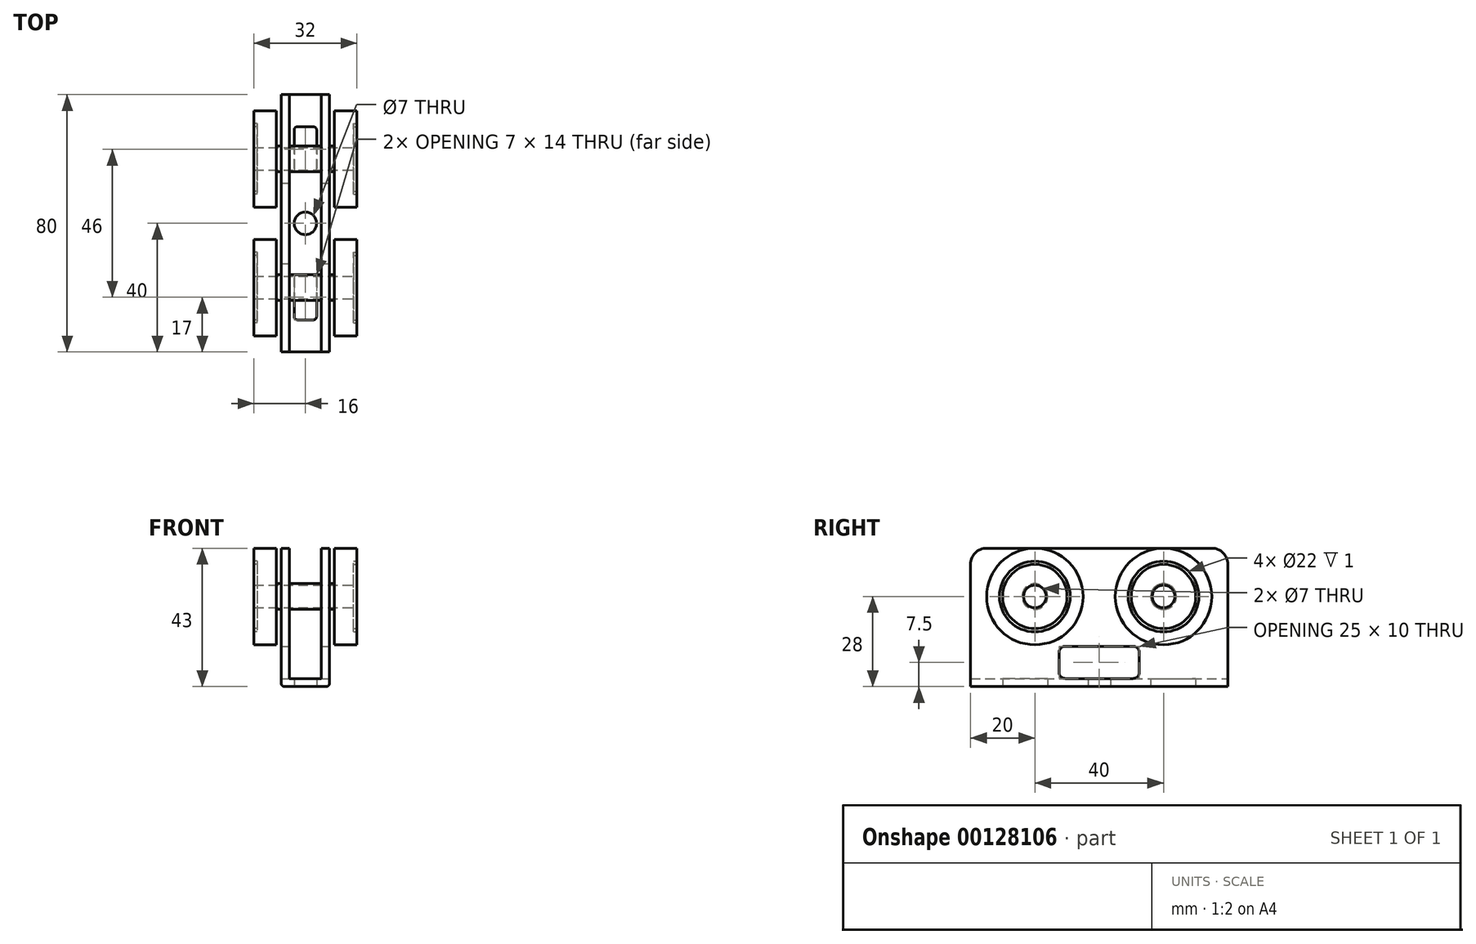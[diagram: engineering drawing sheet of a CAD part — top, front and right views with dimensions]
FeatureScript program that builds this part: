
annotation { "Feature Type Name" : "Feature", "Feature Type Description" : "" }
export const myFeature = defineFeature(function(context is Context, id is Id, definition is map)
    precondition{}
    {
        {
            var Q0;
            Q0=qCreatedBy(makeId("Front.planeOp"),FACE);
            var sketch = newSketch(context, id + "F0", { "sketchPlane" : qUnion([Q0])});
            skLineSegment(sketch, "E0", {"start": v(0, 1) * mm, "end": v(0, 43) * mm});
            skLineSegment(sketch, "E1", {"start": v(1, 0) * mm, "end": v(14, 0) * mm});
            skLineSegment(sketch, "E2", {"start": v(15, 1) * mm, "end": v(15, 43) * mm});
            skLineSegment(sketch, "E3.0", {"start": v(2.5, 2.5) * mm, "end": v(2.5, 43) * mm});
            skLineSegment(sketch, "E3.1", {"start": v(2.5, 2.5) * mm, "end": v(12.5, 2.5) * mm});
            skLineSegment(sketch, "E3.2", {"start": v(12.5, 2.5) * mm, "end": v(12.5, 43) * mm});
            skLineSegment(sketch, "E4", {"start": v(0, 43) * mm, "end": v(2.5, 43) * mm});
            skLineSegment(sketch, "E5", {"start": v(15, 43) * mm, "end": v(12.5, 43) * mm});
            skPoint(sketch, "E6.visualSharp", {"position": v(15, 0) * mm});
            skArc(sketch, "E6.filletArc", {"start": v(14, 0) * mm, "mid": v(14.7, 0.3) * mm, "end": v(15, 1) * mm});
            skPoint(sketch, "E7.visualSharp", {"position": v(0, 0) * mm});
            skArc(sketch, "E7.filletArc", {"start": v(0, 1) * mm, "mid": v(0.3, 0.3) * mm, "end": v(1, 0) * mm});
            skSolve(sketch);
        }
        {
            var Q0;
            Q0 = qSketchRegion(id + "F0", true);
            extrude(context, id + "F1", {"entities" : qUnion([Q0]), "depth" : 80 * mm});
        }
        {
            var Q0;
            Q0=makeQuery(id+"F1.opExtrude","SWEPT_FACE",FACE,{"disambiguationData":[OSD([sQuery(id+"F0.wireOp",EDGE,"E2")])]});
            var sketch = newSketch(context, id + "F2", { "sketchPlane" : qUnion([Q0])});
            skCircle(sketch, "E8", {"center": v(-60, 28) * mm, "radius": 4 * mm});
            skCircle(sketch, "E9", {"center": v(-20, 28) * mm, "radius": 4 * mm});
            skSolve(sketch);
        }
        {
            var Q0;
            Q0 = qSketchRegion(id + "F2", true);
            extrude(context, id + "F3", {"entities" : qUnion([Q0]), "operationType" : NewBodyOperationType.ADD, "depth" : 8.5 * mm});
        }
        {
            var Q0;
            Q0 = qSketchRegion(id + "F2", true);
            extrude(context, id + "F4", {"entities" : qUnion([Q0]), "operationType" : NewBodyOperationType.ADD, "oppositeDirection" : true, "depth" : 23.5 * mm});
        }
        {
            var Q0;
            Q0=makeQuery(id+"F3.opExtrude","CAP_FACE",FACE,{"disambiguationData":[OSD([sQuery(id+"F2.wireOp",EDGE,"E9")])],"isStart":false});
            var sketch = newSketch(context, id + "F5", { "sketchPlane" : qUnion([Q0])});
            skCircle(sketch, "E10", {"center": v(-20, 28) * mm, "radius": 15 * mm});
            skCircle(sketch, "E11", {"center": v(-60, 28) * mm, "radius": 15 * mm});
            skSolve(sketch);
        }
        {
            var Q0;
            Q0 = qSketchRegion(id + "F5", true);
            extrude(context, id + "F6", {"entities" : qUnion([Q0]), "operationType" : NewBodyOperationType.ADD, "oppositeDirection" : true, "depth" : 7 * mm});
        }
        {
            var Q0;
            Q0=makeQuery(id+"F4.opExtrude","CAP_FACE",FACE,{"disambiguationData":[OSD([sQuery(id+"F2.wireOp",EDGE,"E9")])],"isStart":false});
            var sketch = newSketch(context, id + "F7", { "sketchPlane" : qUnion([Q0])});
            skCircle(sketch, "E12", {"center": v(20, 28) * mm, "radius": 15 * mm});
            skCircle(sketch, "E13", {"center": v(60, 28) * mm, "radius": 15 * mm});
            skSolve(sketch);
        }
        {
            var Q0;
            Q0 = qSketchRegion(id + "F7", true);
            extrude(context, id + "F8", {"entities" : qUnion([Q0]), "operationType" : NewBodyOperationType.ADD, "oppositeDirection" : true, "depth" : 7 * mm});
        }
        {
            var Q0;
            Q0=makeQuery(id+"F1.opExtrude","CAP_EDGE",EDGE,{"disambiguationData":[OSD([sQuery(id+"F0.wireOp",EDGE,"E4")])],"isStart":false});
            var Q1;
            Q1=makeQuery(id+"F1.opExtrude","CAP_EDGE",EDGE,{"disambiguationData":[OSD([sQuery(id+"F0.wireOp",EDGE,"E5")])],"isStart":false});
            var Q2;
            Q2=makeQuery(id+"F1.opExtrude","CAP_EDGE",EDGE,{"disambiguationData":[OSD([sQuery(id+"F0.wireOp",EDGE,"E4")])],"isStart":true});
            var Q3;
            Q3=makeQuery(id+"F1.opExtrude","CAP_EDGE",EDGE,{"disambiguationData":[OSD([sQuery(id+"F0.wireOp",EDGE,"E5")])],"isStart":true});
            fillet(context, id + "F9", {"entities" : qUnion([Q0, Q1, Q2, Q3]), "radius" : 5 * mm, "tangentPropagation" : true, "allowEdgeOverflow" : false});
        }
        {
            var Q0;
            Q0=makeQuery(id+"F1.opExtrude","SWEPT_FACE",FACE,{"disambiguationData":[OSD([sQuery(id+"F0.wireOp",EDGE,"E1")])]});
            var sketch = newSketch(context, id + "F10", { "sketchPlane" : qUnion([Q0])});
            skPoint(sketch, "E14.endSnap0", {"position": v(7.5, 0) * mm});
            skCircle(sketch, "E15", {"center": v(7.5, 40) * mm, "radius": 3.5 * mm});
            skSolve(sketch);
        }
        {
            var Q0;
            Q0 = qSketchRegion(id + "F10", true);
            extrude(context, id + "F11", {"entities" : qUnion([Q0]), "operationType" : NewBodyOperationType.REMOVE, "oppositeDirection" : true, "depth" : 25 * mm});
        }
        {
            var Q0;
            Q0=makeQuery(id+"F1.opExtrude","SWEPT_FACE",FACE,{"disambiguationData":[OSD([sQuery(id+"F0.wireOp",EDGE,"E2")])]});
            var sketch = newSketch(context, id + "F12", { "sketchPlane" : qUnion([Q0])});
            skLineSegment(sketch, "E16", {"start": v(-27.5, 4.5) * mm, "end": v(-27.5, 10.5) * mm});
            skLineSegment(sketch, "E17", {"start": v(-29.5, 12.5) * mm, "end": v(-50.5, 12.5) * mm});
            skLineSegment(sketch, "E18", {"start": v(-52.5, 10.5) * mm, "end": v(-52.5, 4.5) * mm});
            skPoint(sketch, "E19.visualSharp", {"position": v(-52.5, 12.5) * mm});
            skArc(sketch, "E19.filletArc", {"start": v(-50.5, 12.5) * mm, "mid": v(-51.91, 11.91) * mm, "end": v(-52.5, 10.5) * mm});
            skArc(sketch, "E20.filletArc", {"start": v(-52.5, 4.5) * mm, "mid": v(-51.91, 3.09) * mm, "end": v(-50.5, 2.5) * mm});
            skArc(sketch, "E21.filletArc", {"start": v(-29.5, 2.5) * mm, "mid": v(-28.09, 3.09) * mm, "end": v(-27.5, 4.5) * mm});
            skPoint(sketch, "E22.visualSharp", {"position": v(-27.5, 12.5) * mm});
            skArc(sketch, "E22.filletArc", {"start": v(-27.5, 10.5) * mm, "mid": v(-28.09, 11.91) * mm, "end": v(-29.5, 12.5) * mm});
            skLineSegment(sketch, "E23", {"start": v(-50.5, 2.5) * mm, "end": v(-29.5, 2.5) * mm});
            skSolve(sketch);
        }
        {
            var Q0;
            Q0 = qSketchRegion(id + "F12", true);
            extrude(context, id + "F13", {"entities" : qUnion([Q0]), "operationType" : NewBodyOperationType.REMOVE, "endBound" : BoundingType.THROUGH_ALL, "oppositeDirection" : true, "depth" : 25 * mm});
        }
        {
            var Q0;
            Q0=makeQuery(id+"F1.opExtrude","SWEPT_FACE",FACE,{"disambiguationData":[OSD([sQuery(id+"F0.wireOp",EDGE,"E1")])]});
            var sketch = newSketch(context, id + "F14", { "sketchPlane" : qUnion([Q0])});
            skLineSegment(sketch, "E24", {"start": v(7.5, 70) * mm, "end": v(5, 70) * mm});
            skLineSegment(sketch, "E25", {"start": v(7.5, 70) * mm, "end": v(10, 70) * mm});
            skLineSegment(sketch, "E26", {"start": v(11, 69) * mm, "end": v(11, 57) * mm});
            skLineSegment(sketch, "E27", {"start": v(4, 69) * mm, "end": v(4, 57) * mm});
            skLineSegment(sketch, "E28", {"start": v(5, 56) * mm, "end": v(10, 56) * mm});
            skLineSegment(sketch, "E29.MirrorCS", {"start": v(11, 11) * mm, "end": v(11, 23) * mm});
            skLineSegment(sketch, "E30.MirrorCS", {"start": v(5, 24) * mm, "end": v(10, 24) * mm});
            skLineSegment(sketch, "E31.MirrorCS", {"start": v(7.5, 10) * mm, "end": v(5, 10) * mm});
            skLineSegment(sketch, "E32.MirrorCS", {"start": v(4, 11) * mm, "end": v(4, 23) * mm});
            skLineSegment(sketch, "E33.MirrorCS", {"start": v(7.5, 10) * mm, "end": v(10, 10) * mm});
            skPoint(sketch, "E34.visualSharp", {"position": v(4, 70) * mm});
            skArc(sketch, "E34.filletArc", {"start": v(5, 70) * mm, "mid": v(4.3, 69.7) * mm, "end": v(4, 69) * mm});
            skPoint(sketch, "E35.visualSharp", {"position": v(11, 70) * mm});
            skArc(sketch, "E35.filletArc", {"start": v(11, 69) * mm, "mid": v(10.7, 69.7) * mm, "end": v(10, 70) * mm});
            skPoint(sketch, "E36.visualSharp", {"position": v(4, 56) * mm});
            skArc(sketch, "E36.filletArc", {"start": v(4, 57) * mm, "mid": v(4.3, 56.3) * mm, "end": v(5, 56) * mm});
            skPoint(sketch, "E37.visualSharp", {"position": v(11, 56) * mm});
            skArc(sketch, "E37.filletArc", {"start": v(10, 56) * mm, "mid": v(10.7, 56.3) * mm, "end": v(11, 57) * mm});
            skPoint(sketch, "E38.visualSharp", {"position": v(11, 24) * mm});
            skArc(sketch, "E38.filletArc", {"start": v(11, 23) * mm, "mid": v(10.7, 23.7) * mm, "end": v(10, 24) * mm});
            skPoint(sketch, "E39.visualSharp", {"position": v(4, 24) * mm});
            skArc(sketch, "E39.filletArc", {"start": v(5, 24) * mm, "mid": v(4.3, 23.7) * mm, "end": v(4, 23) * mm});
            skPoint(sketch, "E40.visualSharp", {"position": v(4, 10) * mm});
            skArc(sketch, "E40.filletArc", {"start": v(4, 11) * mm, "mid": v(4.3, 10.3) * mm, "end": v(5, 10) * mm});
            skPoint(sketch, "E41.visualSharp", {"position": v(11, 10) * mm});
            skArc(sketch, "E41.filletArc", {"start": v(10, 10) * mm, "mid": v(10.7, 10.3) * mm, "end": v(11, 11) * mm});
            skSolve(sketch);
        }
        {
            var Q0;
            Q0 = qSketchRegion(id + "F14", true);
            extrude(context, id + "F15", {"entities" : qUnion([Q0]), "operationType" : NewBodyOperationType.REMOVE, "oppositeDirection" : true, "depth" : 3 * mm});
        }
        {
            var Q0;
            Q0=makeQuery(id+"F8.boolean.opBoolean","MERGE",FACE,{"derivedFrom":[makeQuery(id+"F4.opExtrude","CAP_FACE",FACE,{"disambiguationData":[OSD([sQuery(id+"F2.wireOp",EDGE,"E9")])],"isStart":false}),makeQuery(id+"F8.opExtrude","CAP_FACE",FACE,{"disambiguationData":[OSD([sQuery(id+"F7.wireOp",EDGE,"E12")])],"isStart":true})]});
            var sketch = newSketch(context, id + "F16", { "sketchPlane" : qUnion([Q0])});
            skCircle(sketch, "E42", {"center": v(20, 28) * mm, "radius": 10 * mm});
            skCircle(sketch, "E43", {"center": v(20, 28) * mm, "radius": 11 * mm});
            skCircle(sketch, "E44", {"center": v(60, 28) * mm, "radius": 10 * mm});
            skCircle(sketch, "E45", {"center": v(60, 28) * mm, "radius": 11 * mm});
            skSolve(sketch);
        }
        {
            var Q0;
            Q0 = qSketchRegion(id + "F16", true);
            extrude(context, id + "F17", {"entities" : qUnion([Q0]), "operationType" : NewBodyOperationType.REMOVE, "oppositeDirection" : true, "depth" : 1 * mm});
        }
        {
            var Q0;
            Q0=makeQuery(id+"F6.boolean.opBoolean","MERGE",FACE,{"derivedFrom":[makeQuery(id+"F3.opExtrude","CAP_FACE",FACE,{"disambiguationData":[OSD([sQuery(id+"F2.wireOp",EDGE,"E8")])],"isStart":false}),makeQuery(id+"F6.opExtrude","CAP_FACE",FACE,{"disambiguationData":[OSD([sQuery(id+"F5.wireOp",EDGE,"E11")])],"isStart":true})]});
            var sketch = newSketch(context, id + "F18", { "sketchPlane" : qUnion([Q0])});
            skCircle(sketch, "E46", {"center": v(-60, 28) * mm, "radius": 10 * mm});
            skCircle(sketch, "E47", {"center": v(-60, 28) * mm, "radius": 11 * mm});
            skCircle(sketch, "E48", {"center": v(-20, 28) * mm, "radius": 10 * mm});
            skCircle(sketch, "E49", {"center": v(-20, 28) * mm, "radius": 11 * mm});
            skSolve(sketch);
        }
        {
            var Q0;
            Q0 = qSketchRegion(id + "F18", true);
            extrude(context, id + "F19", {"entities" : qUnion([Q0]), "operationType" : NewBodyOperationType.REMOVE, "oppositeDirection" : true, "depth" : 1 * mm});
        }
        {
            var Q0;
            Q0=makeQuery(id+"F19.boolean.opBoolean","SPLIT",FACE,{"disambiguationData":[TD([makeQuery(id+"F19.opExtrude","SWEPT_FACE",FACE,{"disambiguationData":[OSD([sQuery(id+"F18.wireOp",EDGE,"E48")])]})])],"derivedFrom":makeQuery(id+"F6.boolean.opBoolean","MERGE",FACE,{"derivedFrom":[makeQuery(id+"F3.opExtrude","CAP_FACE",FACE,{"disambiguationData":[OSD([sQuery(id+"F2.wireOp",EDGE,"E9")])],"isStart":false}),makeQuery(id+"F6.opExtrude","CAP_FACE",FACE,{"disambiguationData":[OSD([sQuery(id+"F5.wireOp",EDGE,"E10")])],"isStart":true})]})});
            var sketch = newSketch(context, id + "F20", { "sketchPlane" : qUnion([Q0])});
            skCircle(sketch, "E50", {"center": v(-20, 28) * mm, "radius": 3.5 * mm});
            skCircle(sketch, "E51", {"center": v(-60, 28) * mm, "radius": 3.5 * mm});
            skSolve(sketch);
        }
        {
            var Q0;
            Q0 = qSketchRegion(id + "F20", true);
            extrude(context, id + "F21", {"entities" : qUnion([Q0]), "operationType" : NewBodyOperationType.REMOVE, "endBound" : BoundingType.THROUGH_ALL, "oppositeDirection" : true, "depth" : 25 * mm});
        }
    });
